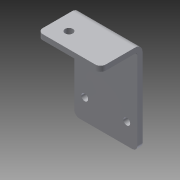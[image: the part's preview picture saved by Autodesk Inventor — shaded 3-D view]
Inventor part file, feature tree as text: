
AUTODESK INVENTOR PART (.ipt)
format: ipt  version: 2014 (Build 180170000, 170)  size: 122,368 bytes
history: native  units: in
note: dims shown in document units (in); Inventor stores cm internally (conversion verified against a paired STEP export)
features: sheet_metal_op x4, sketch x3, other x3, fillet x1
ambient origin geometry x8: Origin, YZ Plane, XZ Plane, XY Plane, X Axis, Y Axis, Z Axis, Center Point
bodies: Solid1 (feature_tree)
feature tree (11):
  sheet_metal_op  "Face1"
  sheet_metal_op  "Flange1"
  fillet  "Fillet1"  Radius=1.5in
  sketch  "Sketch1"  dims[d1=2.0in]
  other  "Plate1"
  sketch  "Sketch2"  dims[d2=0.163in]
  other  "Plate2"
  sheet_metal_op  "Bend1"
  sheet_metal_op  "Corner1"
  sketch  "Sketch4"  dims[d3=0.25in d4=0.7874in d6=1.0in d7=0.3937in d9=1.0in d11=0.125in d12=0.125in d13=0.0625in d14=0.25in d15=0.125in d16=1.0in d17=90.0deg d18=0.05in d19=0.5in d20=0.125in d21=0.125in d22=0.5in d28=0.187in d29=0.375in d30=1.125in d31=0.125in d32=0.0in d33=0.125in]
  other  "Cut2"
